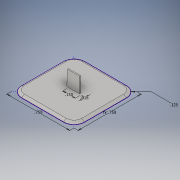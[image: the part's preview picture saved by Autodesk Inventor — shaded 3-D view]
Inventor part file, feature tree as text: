
AUTODESK INVENTOR PART (.ipt)
format: ipt  version: 2016 (Build 200138000, 138)  size: 111,616 bytes
history: native  units: in
note: dims shown in document units (in); Inventor stores cm internally (conversion verified against a paired STEP export)
features: extrude x2, sketch x1
ambient origin geometry x8: Origin, YZ Plane, XZ Plane, XY Plane, X Axis, Y Axis, Z Axis, Center Point
bodies: Solid1 (feature_tree)
feature tree (3):
  sketch  "Sketch1"  dims[d0=0.75in d1=0.75in d2=0.02in d3=-0.4123in d4=0.15in d5=0.0175in d6=0.2in d7=-0.0069in d8=0.125in]
  extrude  "Extrusion1"  Depth=0.125in
  extrude  "Extrusion2"  Depth=0.02in
